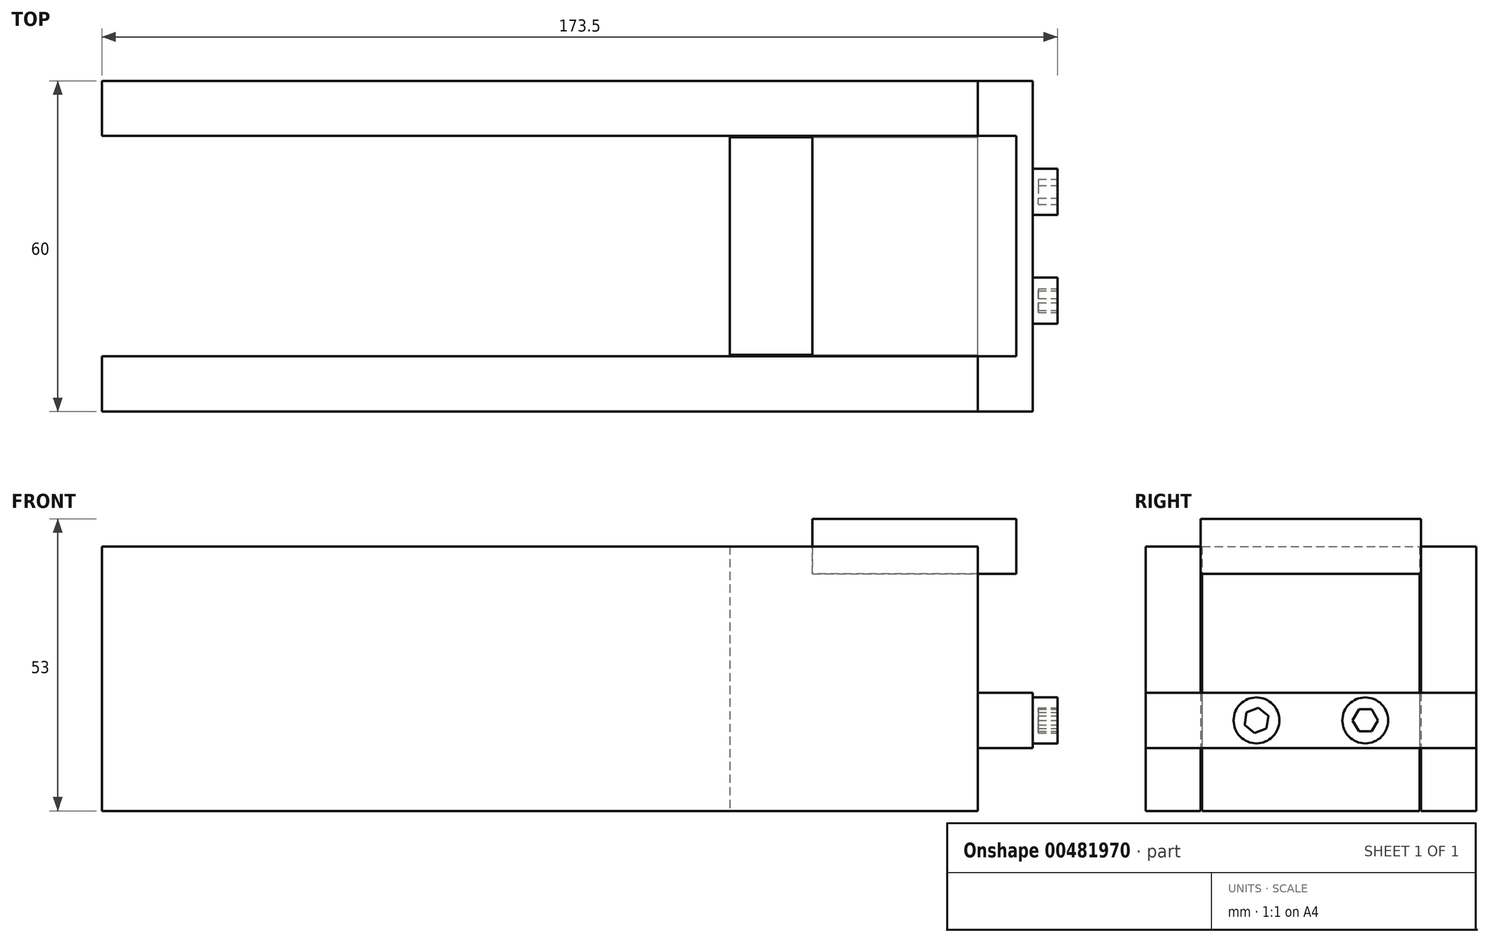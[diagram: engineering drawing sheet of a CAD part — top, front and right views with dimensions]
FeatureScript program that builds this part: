
annotation { "Feature Type Name" : "Feature", "Feature Type Description" : "" }
export const myFeature = defineFeature(function(context is Context, id is Id, definition is map)
    precondition{}
    {
        {
            var Q0;
            Q0=qCreatedBy(makeId("Top.planeOp"),FACE);
            var sketch = newSketch(context, id + "F0", { "sketchPlane" : qUnion([Q0])});
            skLineSegment(sketch, "E0.bottom", {"start": v(-22.5, -19.75) * mm, "end": v(22.5, -19.75) * mm});
            skLineSegment(sketch, "E0.top", {"start": v(-22.5, 19.75) * mm, "end": v(22.5, 19.75) * mm});
            skLineSegment(sketch, "E0.left", {"start": v(-22.5, -19.75) * mm, "end": v(-22.5, 19.75) * mm});
            skLineSegment(sketch, "E0.right", {"start": v(22.5, -19.75) * mm, "end": v(22.5, 19.75) * mm});
            skPoint(sketch, "E0.middle", {"position": v(0, 0) * mm});
            skSolve(sketch);
        }
        {
            var Q0;
            Q0 = qSketchRegion(id + "F0", true);
            extrude(context, id + "F1", {"entities" : qUnion([Q0]), "depth" : 43 * mm});
        }
        {
            var Q0;
            Q0=makeQuery(id+"F1.opExtrude","CAP_FACE",FACE,{"disambiguationData":[OSD([sQuery(id+"F0.wireOp",EDGE,"E0.bottom"),sQuery(id+"F0.wireOp",EDGE,"E0.top"),sQuery(id+"F0.wireOp",EDGE,"E0.left"),sQuery(id+"F0.wireOp",EDGE,"E0.right")])],"isStart":false});
            var sketch = newSketch(context, id + "F2", { "sketchPlane" : qUnion([Q0])});
            skLineSegment(sketch, "E1.bottom", {"start": v(-22.5, 19.75) * mm, "end": v(-7.5, 19.75) * mm});
            skLineSegment(sketch, "E1.top", {"start": v(-22.5, -19.75) * mm, "end": v(-7.5, -19.75) * mm});
            skLineSegment(sketch, "E1.left", {"start": v(-22.5, 19.75) * mm, "end": v(-22.5, -19.75) * mm});
            skLineSegment(sketch, "E1.right", {"start": v(-7.5, 19.75) * mm, "end": v(-7.5, -19.75) * mm});
            skSolve(sketch);
        }
        {
            var Q0;
            Q0 = qSketchRegion(id + "F2", true);
            extrude(context, id + "F3", {"entities" : qUnion([Q0]), "operationType" : NewBodyOperationType.ADD, "depth" : 5 * mm});
        }
        {
            var Q0;
            Q0=makeQuery(id+"F3.opExtrude","SWEPT_FACE",FACE,{"disambiguationData":[OSD([sQuery(id+"F2.wireOp",EDGE,"E1.right")])]});
            var sketch = newSketch(context, id + "F4", { "sketchPlane" : qUnion([Q0])});
            skLineSegment(sketch, "E2.bottom", {"start": v(0, 43) * mm, "end": v(10, 43) * mm});
            skLineSegment(sketch, "E2.top", {"start": v(0, 53) * mm, "end": v(10, 53) * mm});
            skLineSegment(sketch, "E2.left", {"start": v(0, 43) * mm, "end": v(0, 53) * mm});
            skLineSegment(sketch, "E2.right", {"start": v(10, 43) * mm, "end": v(10, 53) * mm});
            skLineSegment(sketch, "E3.bottom", {"start": v(10, 43) * mm, "end": v(20, 43) * mm});
            skLineSegment(sketch, "E3.top", {"start": v(10, 53) * mm, "end": v(20, 53) * mm});
            skLineSegment(sketch, "E3.right", {"start": v(20, 43) * mm, "end": v(20, 53) * mm});
            skLineSegment(sketch, "E4.bottom", {"start": v(0, 43) * mm, "end": v(-10, 43) * mm});
            skLineSegment(sketch, "E4.top", {"start": v(0, 53) * mm, "end": v(-10, 53) * mm});
            skLineSegment(sketch, "E4.right", {"start": v(-10, 43) * mm, "end": v(-10, 53) * mm});
            skLineSegment(sketch, "E5.bottom", {"start": v(-10, 43) * mm, "end": v(-20, 43) * mm});
            skLineSegment(sketch, "E5.top", {"start": v(-10, 53) * mm, "end": v(-20, 53) * mm});
            skLineSegment(sketch, "E5.right", {"start": v(-20, 43) * mm, "end": v(-20, 53) * mm});
            skSolve(sketch);
        }
        {
            var Q0;
            Q0 = qSketchRegion(id + "F4", true);
            extrude(context, id + "F5", {"entities" : qUnion([Q0]), "operationType" : NewBodyOperationType.ADD, "depth" : 37 * mm});
        }
        {
            var Q0;
            Q0=qCreatedBy(makeId("Right.planeOp"),FACE);
            var Q1;
            Q1=makeQuery(id+"F1.opExtrude","CAP_VERTEX",VERTEX,{"disambiguationData":[OSD([sQuery(id+"F0.wireOp",EDGE,"E0.bottom"),sQuery(id+"F0.wireOp",EDGE,"E0.right")])],"isStart":true});
            cPlane(context, id + "F6", {"entities" : qUnion([Q0, Q1]), "cplaneType" : CPlaneType.PLANE_POINT, "offset" : 49.4 * mm, "width" : 150 * mm, "height" : 150 * mm});
        }
        {
            var Q0;
            Q0=qCreatedBy(id+"F6.planeOp",FACE);
            var sketch = newSketch(context, id + "F7", { "sketchPlane" : qUnion([Q0])});
            skLineSegment(sketch, "E6.bottom", {"start": v(20, 48) * mm, "end": v(30, 48) * mm});
            skLineSegment(sketch, "E6.top", {"start": v(20, 0) * mm, "end": v(30, 0) * mm});
            skLineSegment(sketch, "E6.left", {"start": v(20, 48) * mm, "end": v(20, 0) * mm});
            skLineSegment(sketch, "E6.right", {"start": v(30, 48) * mm, "end": v(30, 0) * mm});
            skLineSegment(sketch, "E7.bottom", {"start": v(-20, 48) * mm, "end": v(-30, 48) * mm});
            skLineSegment(sketch, "E7.top", {"start": v(-20, 0) * mm, "end": v(-30, 0) * mm});
            skLineSegment(sketch, "E7.left", {"start": v(-20, 48) * mm, "end": v(-20, 0) * mm});
            skLineSegment(sketch, "E7.right", {"start": v(-30, 48) * mm, "end": v(-30, 0) * mm});
            skSolve(sketch);
        }
        {
            var Q0;
            Q0 = qSketchRegion(id + "F7", true);
            extrude(context, id + "F8", {"entities" : qUnion([Q0]), "oppositeDirection" : true, "depth" : 159 * mm});
        }
        {
            var Q0;
            Q0=makeQuery(id+"F1.opExtrude","SWEPT_FACE",FACE,{"disambiguationData":[OSD([sQuery(id+"F0.wireOp",EDGE,"E0.right")])]});
            var sketch = newSketch(context, id + "F9", { "sketchPlane" : qUnion([Q0])});
            skLineSegment(sketch, "E8.bottom", {"start": v(-30, 21.42) * mm, "end": v(30, 21.42) * mm});
            skLineSegment(sketch, "E8.top", {"start": v(-30, 11.42) * mm, "end": v(30, 11.42) * mm});
            skLineSegment(sketch, "E8.left", {"start": v(-30, 21.42) * mm, "end": v(-30, 11.42) * mm});
            skLineSegment(sketch, "E8.right", {"start": v(30, 21.42) * mm, "end": v(30, 11.42) * mm});
            skSolve(sketch);
        }
        {
            var Q0;
            Q0 = qSketchRegion(id + "F9", true);
            extrude(context, id + "F10", {"entities" : qUnion([Q0]), "depth" : 10 * mm});
        }
        {
            var Q0;
            Q0=makeQuery(id+"F10.opExtrude","CAP_FACE",FACE,{"disambiguationData":[OSD([sQuery(id+"F9.wireOp",EDGE,"E8.bottom"),sQuery(id+"F9.wireOp",EDGE,"E8.top"),sQuery(id+"F9.wireOp",EDGE,"E8.left"),sQuery(id+"F9.wireOp",EDGE,"E8.right")])],"isStart":false});
            var sketch = newSketch(context, id + "F11", { "sketchPlane" : qUnion([Q0])});
            skSolve(sketch);
        }
        {
            var Q0;
            Q0=makeQuery(id+"F11.imprint","IMPRINT",FACE,{"disambiguationData":[TD([[makeQuery(id+"F11.imprint","IMPRINT",EDGE,{"derivedFrom":makeQuery(id+"F10.opExtrude","CAP_EDGE",EDGE,{"disambiguationData":[OSD([sQuery(id+"F9.wireOp",EDGE,"E8.bottom")])],"isStart":false})}),-1.0]])]});
            var sketch = newSketch(context, id + "F12", { "sketchPlane" : qUnion([Q0])});
            skCircle(sketch, "E9", {"center": v(-9.87, 16.42) * mm, "radius": 4.17 * mm});
            skCircle(sketch, "E10", {"center": v(9.88, 16.42) * mm, "radius": 4.17 * mm});
            skSolve(sketch);
        }
        {
            var Q0;
            Q0 = qSketchRegion(id + "F12", true);
            extrude(context, id + "F13", {"entities" : qUnion([Q0]), "depth" : 4.5 * mm});
        }
        {
            var Q0;
            Q0=makeQuery(id+"F13.opExtrude","CAP_FACE",FACE,{"disambiguationData":[OSD([sQuery(id+"F12.wireOp",EDGE,"E9")])],"isStart":false});
            var sketch = newSketch(context, id + "F14", { "sketchPlane" : qUnion([Q0])});
            skCircle(sketch, "E11.cCircle", {"center": v(-9.87, 16.42) * mm, "radius": 2 * mm, "construction": true});
            skLineSegment(sketch, "E11.0", {"start": v(-8.08, 14.97) * mm, "end": v(-10.24, 14.14) * mm});
            skLineSegment(sketch, "E11.1", {"start": v(-10.24, 14.14) * mm, "end": v(-12.03, 15.6) * mm});
            skLineSegment(sketch, "E11.2", {"start": v(-12.03, 15.6) * mm, "end": v(-11.67, 17.88) * mm});
            skLineSegment(sketch, "E11.3", {"start": v(-11.67, 17.88) * mm, "end": v(-9.51, 18.7) * mm});
            skLineSegment(sketch, "E11.4", {"start": v(-9.51, 18.7) * mm, "end": v(-7.72, 17.25) * mm});
            skLineSegment(sketch, "E11.5", {"start": v(-7.72, 17.25) * mm, "end": v(-8.08, 14.97) * mm});
            skPoint(sketch, "E11.0.midPoint", {"position": v(-9.16, 14.56) * mm});
            skCircle(sketch, "E12.cCircle", {"center": v(9.88, 16.42) * mm, "radius": 2 * mm, "construction": true});
            skLineSegment(sketch, "E12.0", {"start": v(11.03, 14.42) * mm, "end": v(8.72, 14.42) * mm});
            skLineSegment(sketch, "E12.1", {"start": v(8.72, 14.42) * mm, "end": v(7.57, 16.42) * mm});
            skLineSegment(sketch, "E12.2", {"start": v(7.57, 16.42) * mm, "end": v(8.72, 18.42) * mm});
            skLineSegment(sketch, "E12.3", {"start": v(8.72, 18.42) * mm, "end": v(11.03, 18.42) * mm});
            skLineSegment(sketch, "E12.4", {"start": v(11.03, 18.42) * mm, "end": v(12.18, 16.42) * mm});
            skLineSegment(sketch, "E12.5", {"start": v(12.18, 16.42) * mm, "end": v(11.03, 14.42) * mm});
            skPoint(sketch, "E12.0.midPoint", {"position": v(9.88, 14.42) * mm});
            skSolve(sketch);
        }
        {
            var Q0;
            Q0 = qSketchRegion(id + "F14", true);
            extrude(context, id + "F15", {"entities" : qUnion([Q0]), "operationType" : NewBodyOperationType.REMOVE, "oppositeDirection" : true, "depth" : 3.5 * mm});
        }
    });
